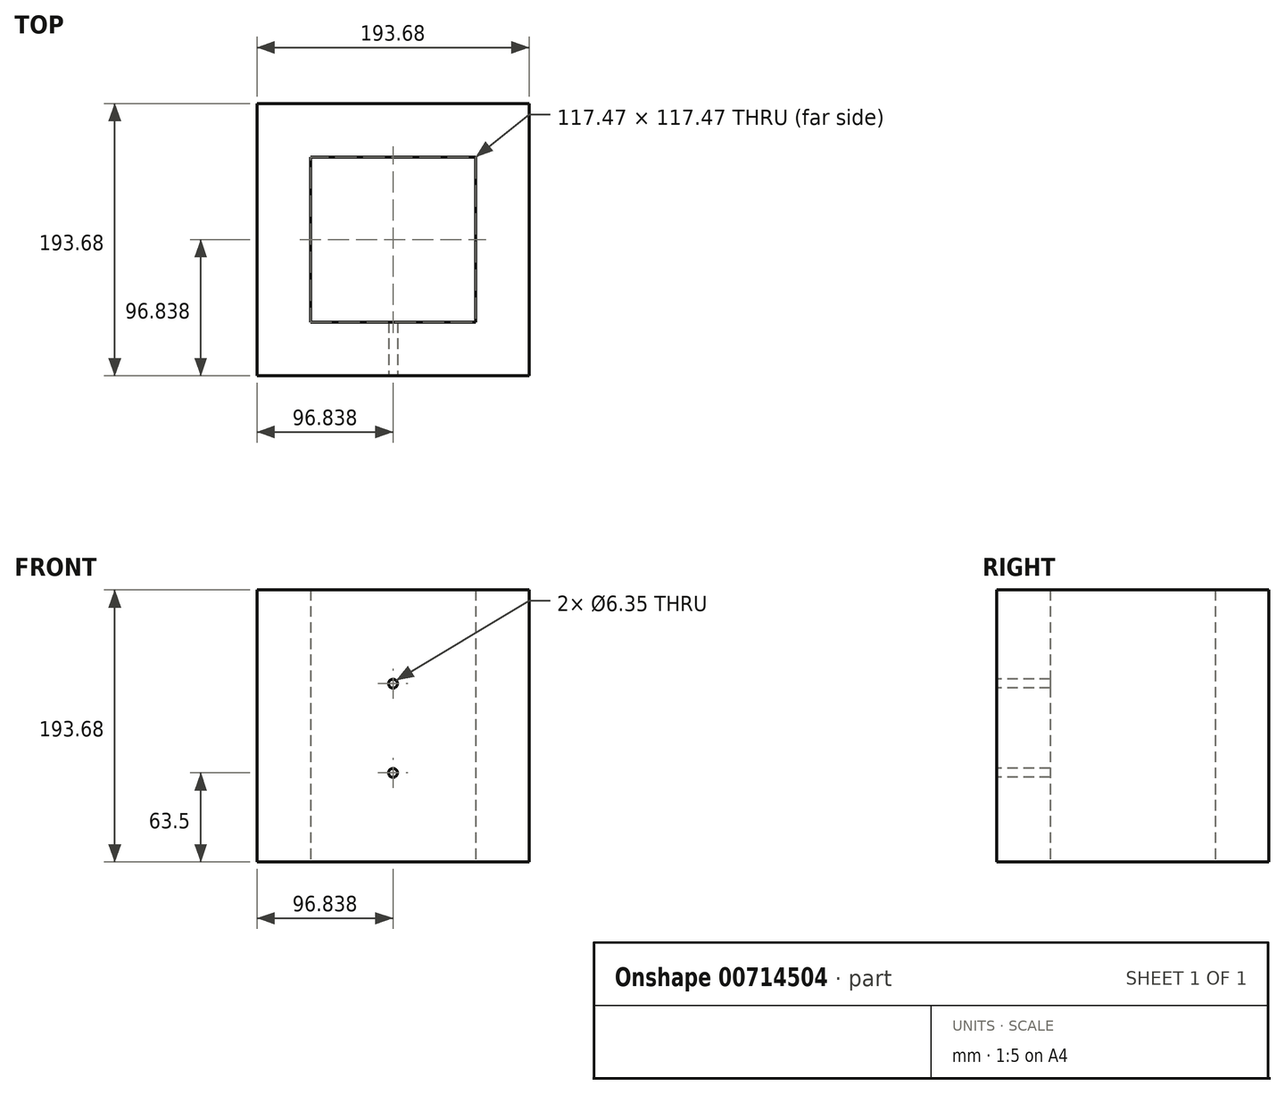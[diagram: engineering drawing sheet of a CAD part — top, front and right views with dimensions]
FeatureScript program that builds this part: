
annotation { "Feature Type Name" : "Feature", "Feature Type Description" : "" }
export const myFeature = defineFeature(function(context is Context, id is Id, definition is map)
    precondition{}
    {
        {
            var Q0;
            Q0=qCreatedBy(makeId("Top.planeOp"),FACE);
            var sketch = newSketch(context, id + "F0", { "sketchPlane" : qUnion([Q0])});
            skLineSegment(sketch, "E0.bottom", {"start": v(0, 0) * mm, "end": v(193.67, 0) * mm});
            skLineSegment(sketch, "E0.top", {"start": v(0, 193.68) * mm, "end": v(193.67, 193.68) * mm});
            skLineSegment(sketch, "E0.left", {"start": v(0, 0) * mm, "end": v(0, 193.68) * mm});
            skLineSegment(sketch, "E0.right", {"start": v(193.67, 0) * mm, "end": v(193.67, 193.68) * mm});
            skLineSegment(sketch, "E1.bottom", {"start": v(38.1, 38.1) * mm, "end": v(155.57, 38.1) * mm});
            skLineSegment(sketch, "E1.top", {"start": v(38.1, 155.58) * mm, "end": v(155.57, 155.58) * mm});
            skLineSegment(sketch, "E1.left", {"start": v(38.1, 38.1) * mm, "end": v(38.1, 155.58) * mm});
            skLineSegment(sketch, "E1.right", {"start": v(155.57, 38.1) * mm, "end": v(155.57, 155.58) * mm});
            skSolve(sketch);
        }
        {
            var Q0;
            Q0=makeQuery(id+"F0.imprint","IMPRINT",FACE,{"disambiguationData":[TD([[makeQuery(id+"F0.imprint","IMPRINT",EDGE,{"derivedFrom":sQuery(id+"F0.wireOp",EDGE,"E0.bottom")}),1.0]])]});
            extrude(context, id + "F1", {"entities" : qUnion([Q0]), "depth" : 193.67 * mm, "offsetDistance" : 25.4 * mm});
        }
        {
            var Q0;
            Q0=makeQuery(id+"F1.opExtrude","SWEPT_FACE",FACE,{"disambiguationData":[OSD([sQuery(id+"F0.wireOp",EDGE,"E0.bottom")])]});
            var sketch = newSketch(context, id + "F2", { "sketchPlane" : qUnion([Q0])});
            skLineSegment(sketch, "E2.bottom", {"start": v(0, 0) * mm, "end": v(193.67, 0) * mm});
            skLineSegment(sketch, "E2.top", {"start": v(0, 38.1) * mm, "end": v(193.67, 38.1) * mm});
            skLineSegment(sketch, "E2.left", {"start": v(0, 0) * mm, "end": v(0, 38.1) * mm});
            skLineSegment(sketch, "E2.right", {"start": v(193.67, 0) * mm, "end": v(193.67, 38.1) * mm});
            skLineSegment(sketch, "E3.0", {"start": v(38.1, 193.68) * mm, "end": v(38.1, 0) * mm});
            skLineSegment(sketch, "E4.0", {"start": v(155.57, 193.68) * mm, "end": v(155.57, 0) * mm});
            skCircle(sketch, "E5", {"center": v(96.84, 63.5) * mm, "radius": 3.18 * mm});
            skPoint(sketch, "E5.centerSnap0", {"position": v(96.84, 38.1) * mm});
            skCircle(sketch, "E6", {"center": v(96.84, 127) * mm, "radius": 3.18 * mm});
            skSolve(sketch);
        }
        {
            var Q0;
            Q0=makeQuery(id+"F2.imprint","IMPRINT",FACE,{"disambiguationData":[TD([[makeQuery(id+"F2.imprint","IMPRINT",EDGE,{"derivedFrom":sQuery(id+"F2.wireOp",EDGE,"E6")}),1.0]])]});
            var Q1;
            Q1=makeQuery(id+"F2.imprint","IMPRINT",FACE,{"disambiguationData":[TD([[makeQuery(id+"F2.imprint","IMPRINT",EDGE,{"derivedFrom":sQuery(id+"F2.wireOp",EDGE,"E5")}),1.0]])]});
            var Q2;
            Q2=makeQuery(id+"F1.opExtrude","SWEPT_FACE",FACE,{"disambiguationData":[OSD([sQuery(id+"F0.wireOp",EDGE,"E1.bottom")])]});
            extrude(context, id + "F3", {"entities" : qUnion([Q0, Q1]), "operationType" : NewBodyOperationType.REMOVE, "endBound" : BoundingType.UP_TO_SURFACE, "oppositeDirection" : true, "depth" : 25.4 * mm, "endBoundEntityFace" : qUnion([Q2]), "offsetDistance" : 25.4 * mm});
        }
    });
